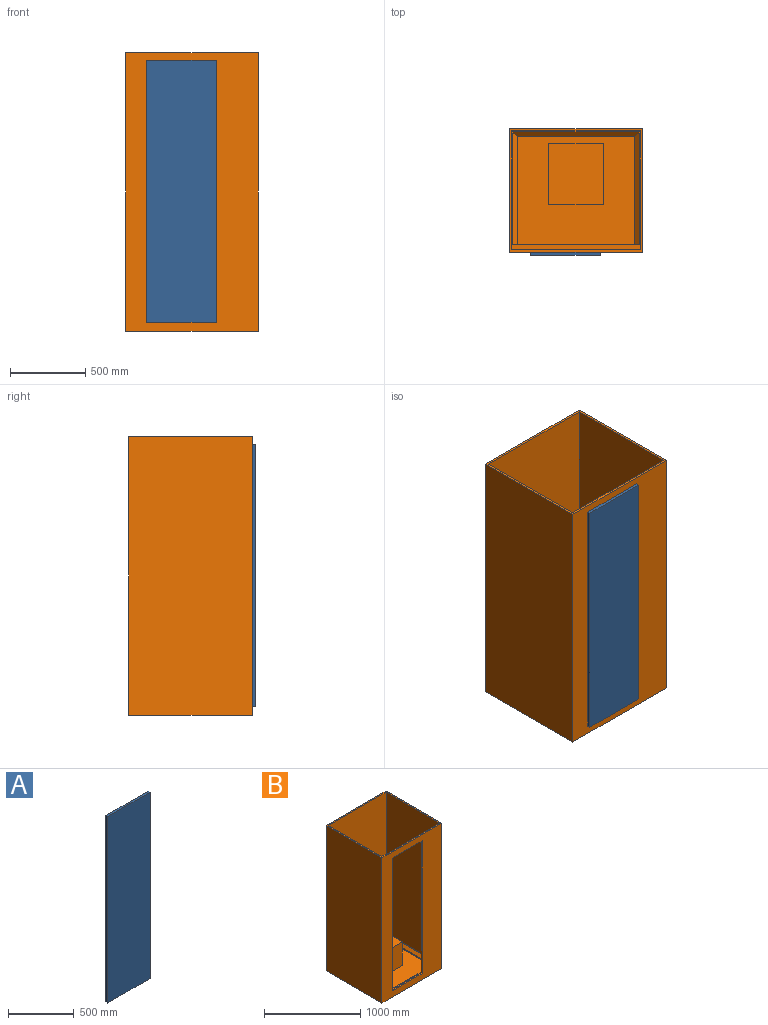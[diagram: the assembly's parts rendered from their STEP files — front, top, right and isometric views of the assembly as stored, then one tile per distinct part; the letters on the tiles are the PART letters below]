
ASSEMBLY  parts=2 mates=1
PART A: 6 faces, bbox 460x20x1740 mm
  f0: plane 1740x20mm, normal (-1,0,0), area 34800mm2, adj f1,f3,f4,f5
  f1: plane 460x20mm, normal (0,0,-1), area 9200mm2, adj f0,f2,f4,f5
  f2: plane 1740x20mm, normal (1,0,0), area 34800mm2, adj f1,f3,f4,f5
  f3: plane 460x20mm, normal (0,0,1), area 9200mm2, adj f0,f2,f4,f5
  f4: plane 1740x460mm, normal (0,-1,0), area 800400mm2, adj f0,f1,f2,f3
  f5: plane 1740x460mm, normal (0,1,0), area 800400mm2, adj f0,f1,f2,f3
PART B: 28 faces, bbox 880x820x1850 mm
  f0: plane 1795x850mm, normal (0,1,0), area 782150mm2, adj f2,f4,f9,f10,f19,f20,f21,f22
  f1: plane 1850x880mm, normal (0,-1,0), area 884400mm2, adj f4,f5,f6,f7,f19,f20,f21,f22
  f2: plane 850x790mm, normal (0,0,1), area 41500mm2, adj f0,f3,f9,f10,f13,f16,f17,f18
  f3: plane 1795x850mm, normal (0,-1,0), area 1525750mm2, adj f2,f4,f9,f10
  f4: plane 880x820mm, normal (0,0,1), area 50100mm2, adj f0,f1,f3,f5,f7,f8,f9,f10
  f5: plane 1850x820mm, normal (-1,0,0), area 1517000mm2, adj f1,f4,f6,f8
  f6: plane 880x820mm, normal (0,0,-1), area 721600mm2, adj f1,f5,f7,f8
  f7: plane 1850x820mm, normal (1,0,0), area 1517000mm2, adj f1,f4,f6,f8
  f8: plane 1850x880mm, normal (0,1,0), area 1628000mm2, adj f4,f5,f6,f7
  f9: plane 1795x790mm, normal (1,0,0), area 1418050mm2, adj f0,f2,f3,f4
  f10: plane 1795x790mm, normal (-1,0,0), area 1418050mm2, adj f0,f2,f3,f4
  f11: plane 720x15mm, normal (1,0,0), area 10800mm2, adj f13,f14,f15,f16
  f12: plane 720x15mm, normal (-1,0,0), area 10800mm2, adj f13,f14,f15,f18
  f13: plane 840x45mm, normal (0,1,0), area 36000mm2, adj f2,f11,f12,f15,f16,f18
  f14: plane 780x15mm, normal (0,-1,0), area 11700mm2, adj f11,f12,f15,f17
  f15: plane 780x720mm, normal (0,0,1), area 417600mm2, adj f11,f12,f13,f14,f23,f24,f25,f26
  f16: plane 750x30mm, normal (0.71,0,0.71), area 31183.4mm2, adj f2,f11,f13,f17
  f17: plane 840x30mm, normal (0,-0.71,0.71), area 34365.4mm2, adj f2,f14,f16,f18
  f18: plane 750x30mm, normal (-0.71,0,0.71), area 31183.4mm2, adj f2,f12,f13,f17
  f19: plane 440x15mm, normal (0,0,-1), area 6600mm2, adj f0,f1,f20,f22
  f20: plane 1690x15mm, normal (1,0,0), area 25350mm2, adj f0,f1,f19,f21
  f21: plane 440x15mm, normal (0,0,1), area 6600mm2, adj f0,f1,f20,f22
  f22: plane 1690x15mm, normal (-1,0,0), area 25350mm2, adj f0,f1,f19,f21
  f23: plane 400x300mm, normal (1,0,0), area 120000mm2, adj f15,f24,f26,f27
  f24: plane 360x300mm, normal (0,1,0), area 108000mm2, adj f15,f23,f25,f27
  f25: plane 400x300mm, normal (-1,0,0), area 120000mm2, adj f15,f24,f26,f27
  f26: plane 360x300mm, normal (0,-1,0), area 108000mm2, adj f15,f23,f25,f27
  f27: plane 400x360mm, normal (0,0,1), area 144000mm2, adj f23,f24,f25,f26
PLACE A t=(-191.74,100.14,-213.55)mm
PLACE B t=(-331.74,920.14,-273.55)mm
MATE fastened A.f5 <-> B.f1  axis (0,1,0) through (268.26,100.14,1526.45)mm
